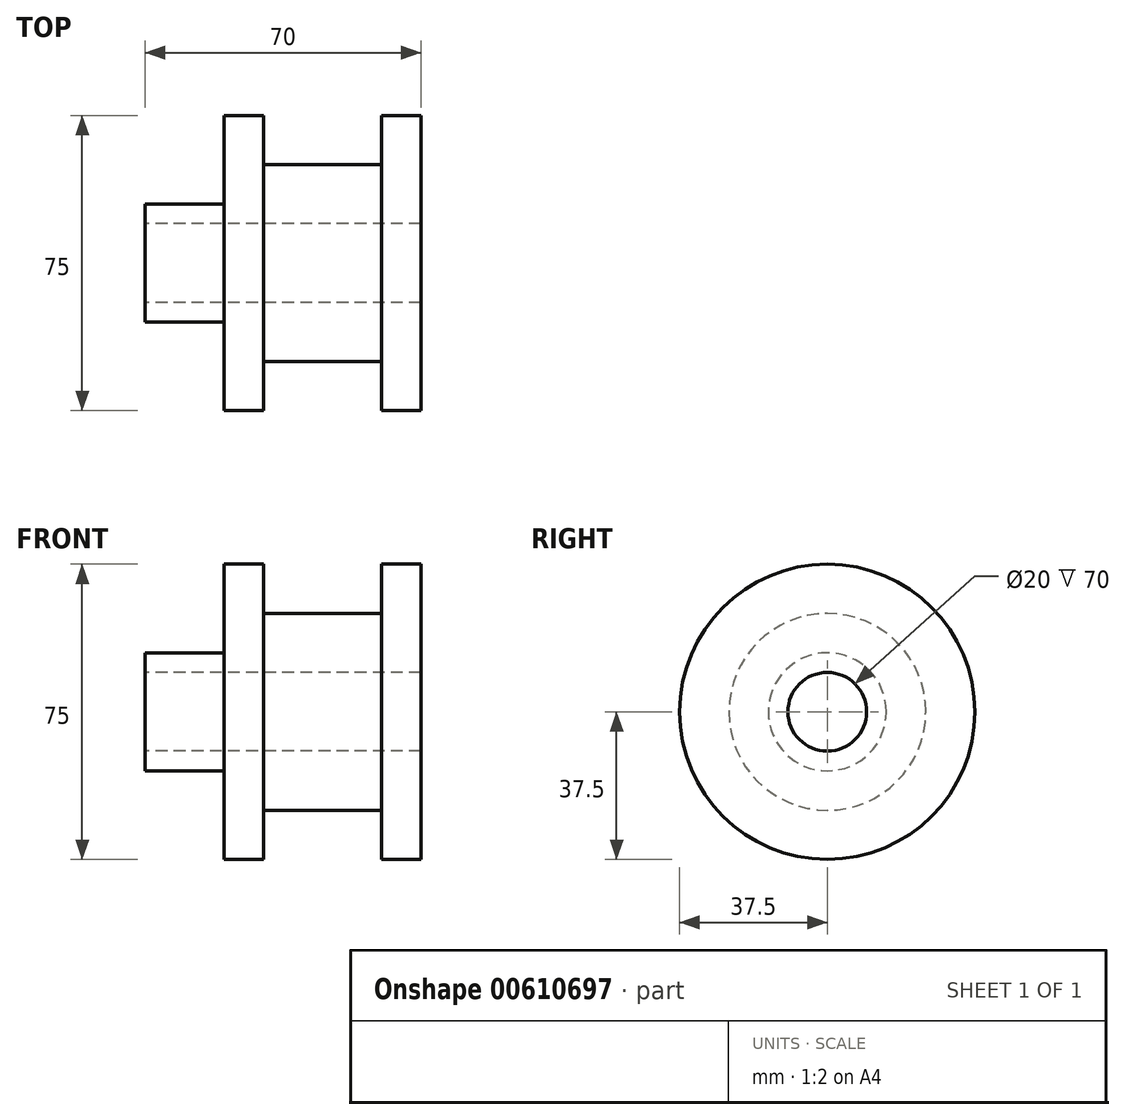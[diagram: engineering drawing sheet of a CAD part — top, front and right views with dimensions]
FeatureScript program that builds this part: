
annotation { "Feature Type Name" : "Feature", "Feature Type Description" : "" }
export const myFeature = defineFeature(function(context is Context, id is Id, definition is map)
    precondition{}
    {
        {
            var Q0;
            Q0=qCreatedBy(makeId("Right.planeOp"),FACE);
            var sketch = newSketch(context, id + "F0", { "sketchPlane" : qUnion([Q0])});
            skCircle(sketch, "E0", {"center": v(0, 0) * mm, "radius": 10 * mm});
            skCircle(sketch, "E1", {"center": v(0, 0) * mm, "radius": 15 * mm});
            skSolve(sketch);
        }
        {
            var Q0;
            Q0 = qSketchRegion(id + "F0", true);
            extrude(context, id + "F1", {"entities" : qUnion([Q0]), "depth" : 20 * mm, "offsetDistance" : 25 * mm});
        }
        {
            var Q0;
            Q0=makeQuery(id+"F1.opExtrude","CAP_FACE",FACE,{"disambiguationData":[OSD([sQuery(id+"F0.wireOp",EDGE,"E0"),sQuery(id+"F0.wireOp",EDGE,"E1")])],"isStart":false});
            var sketch = newSketch(context, id + "F2", { "sketchPlane" : qUnion([Q0])});
            skCircle(sketch, "E2", {"center": v(0, 0) * mm, "radius": 37.5 * mm});
            skSolve(sketch);
        }
        {
            var Q0;
            Q0=makeQuery(id+"F2.imprint","IMPRINT",FACE,{"disambiguationData":[TD([[makeQuery(id+"F2.imprint","IMPRINT",EDGE,{"derivedFrom":sQuery(id+"F2.wireOp",EDGE,"E2")}),1.0]])]});
            var Q1;
            Q1=makeQuery(id+"F2.imprint","IMPRINT",FACE,{"disambiguationData":[TD([[makeQuery(id+"F2.imprint","IMPRINT",EDGE,{"derivedFrom":makeQuery(id+"F1.opExtrude","CAP_EDGE",EDGE,{"disambiguationData":[OSD([sQuery(id+"F0.wireOp",EDGE,"E0")])],"isStart":false})}),-1.0]])]});
            extrude(context, id + "F3", {"entities" : qUnion([Q0, Q1]), "operationType" : NewBodyOperationType.ADD, "depth" : 10 * mm, "offsetDistance" : 25 * mm});
        }
        {
            var Q0;
            Q0=makeQuery(id+"F3.opExtrude","CAP_FACE",FACE,{"disambiguationData":[OSD([sQuery(id+"F0.wireOp",EDGE,"E0"),sQuery(id+"F2.wireOp",EDGE,"E2")])],"isStart":false});
            var sketch = newSketch(context, id + "F4", { "sketchPlane" : qUnion([Q0])});
            skCircle(sketch, "E3", {"center": v(0, 0) * mm, "radius": 25 * mm});
            skSolve(sketch);
        }
        {
            var Q0;
            Q0=makeQuery(id+"F4.imprint","IMPRINT",FACE,{"disambiguationData":[TD([[makeQuery(id+"F4.imprint","IMPRINT",EDGE,{"derivedFrom":sQuery(id+"F4.wireOp",EDGE,"E3")}),1.0]])]});
            extrude(context, id + "F5", {"entities" : qUnion([Q0]), "operationType" : NewBodyOperationType.ADD, "depth" : 30 * mm, "offsetDistance" : 25 * mm});
        }
        {
            var Q0;
            Q0=makeQuery(id+"F5.opExtrude","CAP_FACE",FACE,{"disambiguationData":[OSD([sQuery(id+"F0.wireOp",EDGE,"E0"),sQuery(id+"F4.wireOp",EDGE,"E3")])],"isStart":false});
            var sketch = newSketch(context, id + "F6", { "sketchPlane" : qUnion([Q0])});
            skCircle(sketch, "E4", {"center": v(0, 0) * mm, "radius": 37.5 * mm});
            skSolve(sketch);
        }
        {
            var Q0;
            Q0=makeQuery(id+"F6.imprint","IMPRINT",FACE,{"disambiguationData":[TD([[makeQuery(id+"F6.imprint","IMPRINT",EDGE,{"derivedFrom":sQuery(id+"F6.wireOp",EDGE,"E4")}),1.0]])]});
            var Q1;
            Q1=makeQuery(id+"F6.imprint","IMPRINT",FACE,{"disambiguationData":[TD([[makeQuery(id+"F6.imprint","IMPRINT",EDGE,{"derivedFrom":makeQuery(id+"F5.opExtrude","CAP_EDGE",EDGE,{"disambiguationData":[OSD([sQuery(id+"F4.wireOp",EDGE,"E3")])],"isStart":false})}),1.0]])]});
            extrude(context, id + "F7", {"entities" : qUnion([Q0, Q1]), "operationType" : NewBodyOperationType.ADD, "depth" : 10 * mm, "offsetDistance" : 25 * mm});
        }
    });
